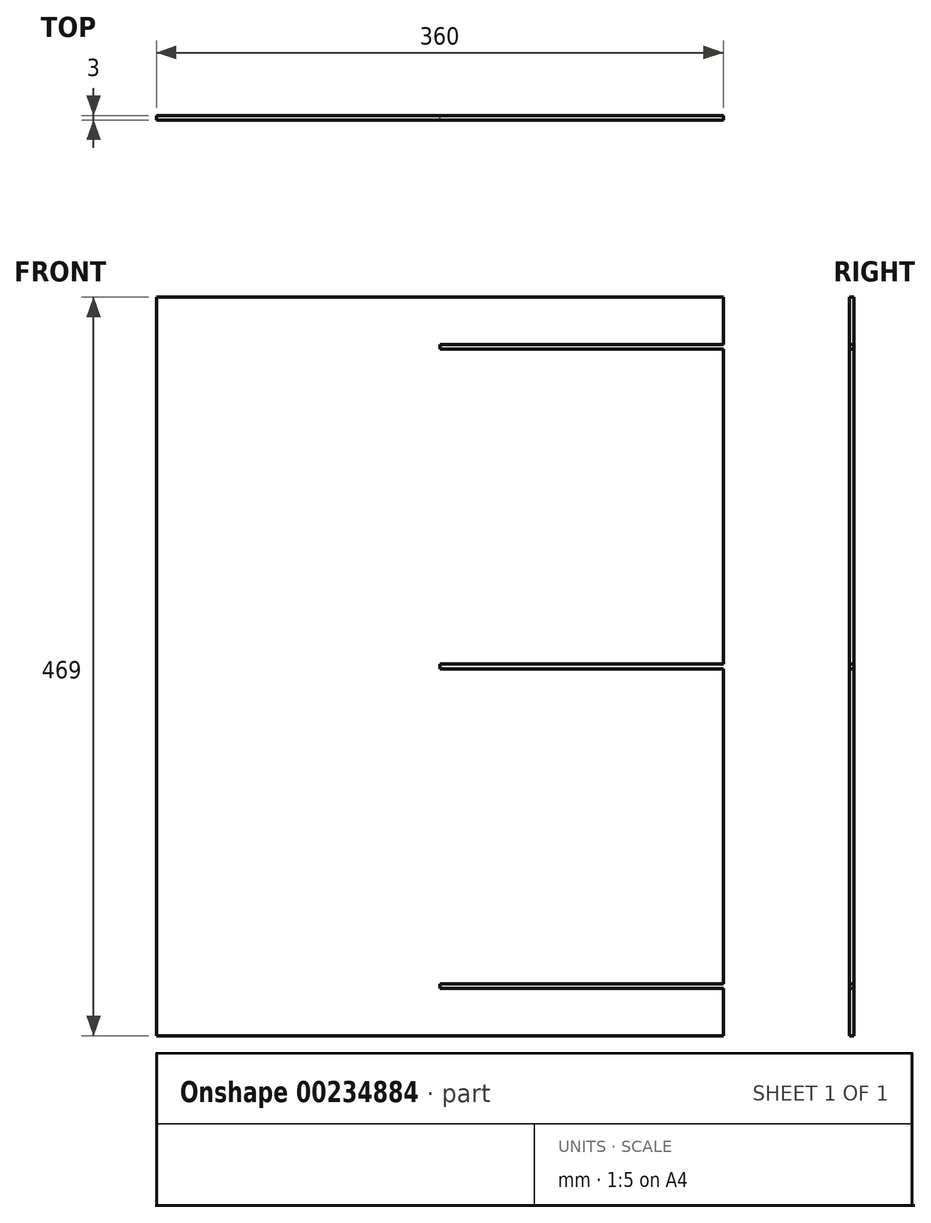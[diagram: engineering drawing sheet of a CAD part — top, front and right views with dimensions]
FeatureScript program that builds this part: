
annotation { "Feature Type Name" : "Feature", "Feature Type Description" : "" }
export const myFeature = defineFeature(function(context is Context, id is Id, definition is map)
    precondition{}
    {
        {
            var Q0;
            Q0=qCreatedBy(makeId("Front.planeOp"),FACE);
            var sketch = newSketch(context, id + "F0", { "sketchPlane" : qUnion([Q0])});
            skLineSegment(sketch, "E0.bottom", {"start": v(53.16, 63.33) * mm, "end": v(413.16, 63.33) * mm, "construction": true});
            skLineSegment(sketch, "E0.top", {"start": v(233.16, 263.33) * mm, "end": v(413.16, 263.33) * mm});
            skLineSegment(sketch, "E0.right", {"start": v(413.16, 63.33) * mm, "end": v(413.16, 263.33) * mm});
            skLineSegment(sketch, "E1", {"start": v(233.16, 263.33) * mm, "end": v(233.16, 266.33) * mm});
            skLineSegment(sketch, "E2.0.1.0", {"start": v(233.16, 266.33) * mm, "end": v(413.16, 266.33) * mm});
            skLineSegment(sketch, "E2.0.1.1", {"start": v(413.16, 266.33) * mm, "end": v(413.16, 466.33) * mm});
            skLineSegment(sketch, "E2.0.1.2", {"start": v(233.16, 466.33) * mm, "end": v(413.16, 466.33) * mm});
            skLineSegment(sketch, "E2.0.1.3", {"start": v(233.16, 466.33) * mm, "end": v(233.16, 469.33) * mm});
            skLineSegment(sketch, "E2.0.2.0", {"start": v(233.16, 469.33) * mm, "end": v(413.16, 469.33) * mm});
            skLineSegment(sketch, "E2.0.2.1", {"start": v(413.16, 469.33) * mm, "end": v(413.16, 669.33) * mm});
            skLineSegment(sketch, "E2.0.2.2", {"start": v(233.16, 669.33) * mm, "end": v(413.16, 669.33) * mm});
            skLineSegment(sketch, "E2.0.2.3", {"start": v(233.16, 669.33) * mm, "end": v(233.16, 672.33) * mm});
            skLineSegment(sketch, "E2.0.3.0", {"start": v(233.16, 672.33) * mm, "end": v(413.16, 672.33) * mm});
            skLineSegment(sketch, "E2.0.3.1", {"start": v(413.16, 672.33) * mm, "end": v(413.16, 872.33) * mm});
            skLineSegment(sketch, "E2.direction1", {"start": v(53.16, 63.33) * mm, "end": v(159.12, 63.33) * mm, "construction": true});
            skLineSegment(sketch, "E2.direction2", {"start": v(53.16, 63.33) * mm, "end": v(53.16, 266.33) * mm, "construction": true});
            skLineSegment(sketch, "E3", {"start": v(53.16, 63.33) * mm, "end": v(53.16, 872.33) * mm});
            skPoint(sketch, "E4.orphan", {"position": v(53.16, 672.33) * mm});
            skPoint(sketch, "E5.orphan", {"position": v(53.16, 469.33) * mm});
            skPoint(sketch, "E2.0.3.2.start.orphan", {"position": v(193.16, 872.33) * mm});
            skLineSegment(sketch, "E6", {"start": v(53.16, 872.33) * mm, "end": v(413.16, 872.33) * mm, "construction": true});
            skLineSegment(sketch, "E7", {"start": v(413.16, 702.33) * mm, "end": v(53.16, 702.33) * mm});
            skLineSegment(sketch, "E8", {"start": v(413.16, 233.33) * mm, "end": v(53.16, 233.33) * mm});
            skSolve(sketch);
        }
        {
            var Q0;
            Q0=makeQuery(id+"F0.imprint","IMPRINT",FACE,{"disambiguationData":[TD([[makeQuery(id+"F0.imprint","IMPRINT",EDGE,{"derivedFrom":sQuery(id+"F0.wireOp",EDGE,"E0.bottom")}),1.0]])]});
            var Q1;
            {var subQ0=sQuery(id+"F0.wireOp",EDGE,"E0.top");Q1=makeQuery(id+"F0.imprint","IMPRINT",FACE,{"disambiguationData":[TD([[makeQuery(id+"F0.imprint","IMPRINT",EDGE,{"derivedFrom":subQ0}),-1.0]])]});}
            extrude(context, id + "F1", {"entities" : qUnion([Q0, Q1]), "depth" : 3 * mm});
        }
    });
